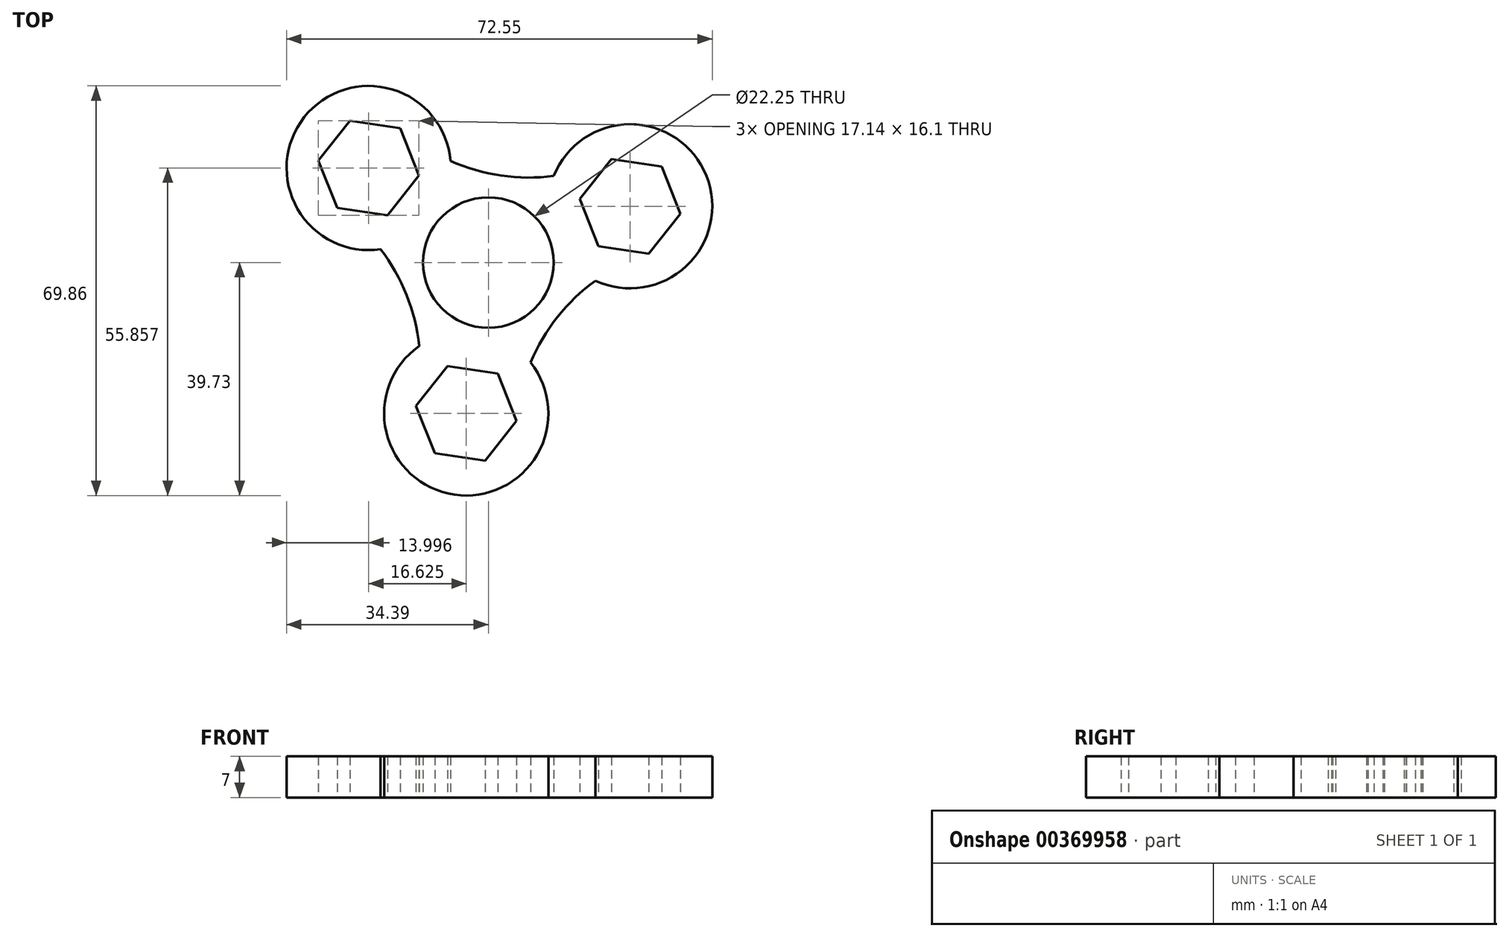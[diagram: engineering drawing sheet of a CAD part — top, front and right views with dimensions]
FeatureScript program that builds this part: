
annotation { "Feature Type Name" : "Feature", "Feature Type Description" : "" }
export const myFeature = defineFeature(function(context is Context, id is Id, definition is map)
    precondition{}
    {
        {
            var Q0;
            Q0=qCreatedBy(makeId("Top.planeOp"),FACE);
            var sketch = newSketch(context, id + "F0", { "sketchPlane" : qUnion([Q0])});
            skCircle(sketch, "E0", {"center": v(0, 0) * mm, "radius": 15 * mm});
            skCircle(sketch, "E1", {"center": v(0, 0) * mm, "radius": 11.12 * mm});
            skLineSegment(sketch, "E2", {"start": v(0, 0) * mm, "end": v(-20.4, 16.13) * mm});
            skLineSegment(sketch, "E3", {"start": v(0, 0) * mm, "end": v(24.16, 9.6) * mm});
            skLineSegment(sketch, "E4", {"start": v(0, 0) * mm, "end": v(-3.77, -25.73) * mm});
            skCircle(sketch, "E5.cCircle", {"center": v(-20.4, 16.13) * mm, "radius": 7.5 * mm, "construction": true});
            skLineSegment(sketch, "E5.0", {"start": v(-11.83, 14.87) * mm, "end": v(-17.2, 8.08) * mm});
            skLineSegment(sketch, "E5.1", {"start": v(-17.2, 8.08) * mm, "end": v(-25.77, 9.33) * mm});
            skLineSegment(sketch, "E5.2", {"start": v(-25.77, 9.33) * mm, "end": v(-28.96, 17.38) * mm});
            skLineSegment(sketch, "E5.3", {"start": v(-28.96, 17.38) * mm, "end": v(-23.6, 24.18) * mm});
            skLineSegment(sketch, "E5.4", {"start": v(-23.6, 24.18) * mm, "end": v(-15.02, 22.92) * mm});
            skLineSegment(sketch, "E5.5", {"start": v(-15.02, 22.92) * mm, "end": v(-11.83, 14.87) * mm});
            skPoint(sketch, "E5.0.midPoint", {"position": v(-14.51, 11.47) * mm});
            skCircle(sketch, "E6.cCircle", {"center": v(24.16, 9.6) * mm, "radius": 7.5 * mm, "construction": true});
            skLineSegment(sketch, "E6.0", {"start": v(18.8, 2.8) * mm, "end": v(15.6, 10.85) * mm});
            skLineSegment(sketch, "E6.1", {"start": v(15.6, 10.85) * mm, "end": v(20.97, 17.65) * mm});
            skLineSegment(sketch, "E6.2", {"start": v(20.97, 17.65) * mm, "end": v(29.54, 16.4) * mm});
            skLineSegment(sketch, "E6.3", {"start": v(29.54, 16.4) * mm, "end": v(32.73, 8.34) * mm});
            skLineSegment(sketch, "E6.4", {"start": v(32.73, 8.34) * mm, "end": v(27.36, 1.55) * mm});
            skLineSegment(sketch, "E6.5", {"start": v(27.36, 1.55) * mm, "end": v(18.8, 2.8) * mm});
            skPoint(sketch, "E6.0.midPoint", {"position": v(17.2, 6.83) * mm});
            skCircle(sketch, "E7.cCircle", {"center": v(-3.77, -25.73) * mm, "radius": 7.5 * mm, "construction": true});
            skLineSegment(sketch, "E7.0", {"start": v(-6.97, -17.68) * mm, "end": v(1.6, -18.93) * mm});
            skLineSegment(sketch, "E7.1", {"start": v(1.6, -18.93) * mm, "end": v(4.8, -26.98) * mm});
            skLineSegment(sketch, "E7.2", {"start": v(4.8, -26.98) * mm, "end": v(-0.57, -33.77) * mm});
            skLineSegment(sketch, "E7.3", {"start": v(-0.57, -33.77) * mm, "end": v(-9.14, -32.52) * mm});
            skLineSegment(sketch, "E7.4", {"start": v(-9.14, -32.52) * mm, "end": v(-12.34, -24.47) * mm});
            skLineSegment(sketch, "E7.5", {"start": v(-12.34, -24.47) * mm, "end": v(-6.97, -17.68) * mm});
            skPoint(sketch, "E7.0.midPoint", {"position": v(-2.68, -18.3) * mm});
            skArc(sketch, "E8", {"start": v(-15.02, 22.92) * mm, "mid": v(2.17, 14.84) * mm, "end": v(20.97, 17.65) * mm});
            skArc(sketch, "E9", {"start": v(27.36, 1.55) * mm, "mid": v(11.77, -9.3) * mm, "end": v(4.8, -26.98) * mm});
            skArc(sketch, "E10", {"start": v(-12.34, -24.47) * mm, "mid": v(-13.94, -5.54) * mm, "end": v(-25.77, 9.33) * mm});
            skCircle(sketch, "E11", {"center": v(-3.77, -25.73) * mm, "radius": 14 * mm});
            skCircle(sketch, "E12", {"center": v(-20.4, 16.13) * mm, "radius": 14 * mm});
            skCircle(sketch, "E13", {"center": v(24.16, 9.6) * mm, "radius": 14 * mm});
            skSolve(sketch);
        }
        {
            var Q0;
            {var subQ0=sQuery(id+"F0.wireOp",EDGE,"E8");var subQ1=sQuery(id+"F0.wireOp",EDGE,"E0");var subQ2=makeQuery(id+"F0.imprint","INTERSECT",VERTEX,{"derivedFrom":[subQ1,subQ0]});Q0=makeQuery(id+"F0.imprint","IMPRINT",FACE,{"disambiguationData":[TD([[makeQuery(id+"F0.imprint","IMPRINT",EDGE,{"disambiguationData":[TD([[subQ2,1.0]])],"derivedFrom":subQ1}),-1.0]])]});}
            var Q1;
            {var subQ0=sQuery(id+"F0.wireOp",EDGE,"E8");var subQ1=sQuery(id+"F0.wireOp",EDGE,"E0");var subQ2=makeQuery(id+"F0.imprint","INTERSECT",VERTEX,{"derivedFrom":[subQ1,subQ0]});Q1=makeQuery(id+"F0.imprint","IMPRINT",FACE,{"disambiguationData":[TD([[makeQuery(id+"F0.imprint","IMPRINT",EDGE,{"disambiguationData":[TD([[subQ2,-1.0]])],"derivedFrom":subQ1}),-1.0]])]});}
            var Q2;
            {var subQ0=sQuery(id+"F0.wireOp",EDGE,"E10");var subQ1=sQuery(id+"F0.wireOp",EDGE,"E0");var subQ2=makeQuery(id+"F0.imprint","INTERSECT",VERTEX,{"derivedFrom":[subQ1,subQ0]});Q2=makeQuery(id+"F0.imprint","IMPRINT",FACE,{"disambiguationData":[TD([[makeQuery(id+"F0.imprint","IMPRINT",EDGE,{"disambiguationData":[TD([[subQ2,1.0]])],"derivedFrom":subQ1}),-1.0]])]});}
            var Q3;
            {var subQ0=sQuery(id+"F0.wireOp",EDGE,"E10");var subQ1=sQuery(id+"F0.wireOp",EDGE,"E0");var subQ2=makeQuery(id+"F0.imprint","INTERSECT",VERTEX,{"derivedFrom":[subQ1,subQ0]});Q3=makeQuery(id+"F0.imprint","IMPRINT",FACE,{"disambiguationData":[TD([[makeQuery(id+"F0.imprint","IMPRINT",EDGE,{"disambiguationData":[TD([[subQ2,-1.0]])],"derivedFrom":subQ1}),-1.0]])]});}
            var Q4;
            {var subQ0=sQuery(id+"F0.wireOp",EDGE,"E9");var subQ1=sQuery(id+"F0.wireOp",EDGE,"E0");var subQ2=makeQuery(id+"F0.imprint","INTERSECT",VERTEX,{"derivedFrom":[subQ1,subQ0]});Q4=makeQuery(id+"F0.imprint","IMPRINT",FACE,{"disambiguationData":[TD([[makeQuery(id+"F0.imprint","IMPRINT",EDGE,{"disambiguationData":[TD([[subQ2,1.0]])],"derivedFrom":subQ1}),-1.0]])]});}
            var Q5;
            {var subQ0=sQuery(id+"F0.wireOp",EDGE,"E9");var subQ1=sQuery(id+"F0.wireOp",EDGE,"E0");var subQ2=makeQuery(id+"F0.imprint","INTERSECT",VERTEX,{"derivedFrom":[subQ1,subQ0]});Q5=makeQuery(id+"F0.imprint","IMPRINT",FACE,{"disambiguationData":[TD([[makeQuery(id+"F0.imprint","IMPRINT",EDGE,{"disambiguationData":[TD([[subQ2,-1.0]])],"derivedFrom":subQ1}),-1.0]])]});}
            var Q6;
            {var subQ5=sQuery(id+"F0.wireOp",EDGE,"E5.2");Q6=makeQuery(id+"F0.imprint","IMPRINT",FACE,{"disambiguationData":[TD([[makeQuery(id+"F0.imprint","IMPRINT",EDGE,{"derivedFrom":subQ5}),1.0]])]});}
            var Q7;
            {var subQ1=sQuery(id+"F0.wireOp",EDGE,"E6.2");Q7=makeQuery(id+"F0.imprint","IMPRINT",FACE,{"disambiguationData":[TD([[makeQuery(id+"F0.imprint","IMPRINT",EDGE,{"derivedFrom":subQ1}),1.0]])]});}
            var Q8;
            {var subQ2=sQuery(id+"F0.wireOp",EDGE,"E7.2");Q8=makeQuery(id+"F0.imprint","IMPRINT",FACE,{"disambiguationData":[TD([[makeQuery(id+"F0.imprint","IMPRINT",EDGE,{"derivedFrom":subQ2}),1.0]])]});}
            var Q9;
            {var subQ0=sQuery(id+"F0.wireOp",EDGE,"E6.5");Q9=makeQuery(id+"F0.imprint","IMPRINT",FACE,{"disambiguationData":[TD([[makeQuery(id+"F0.imprint","IMPRINT",EDGE,{"derivedFrom":subQ0}),1.0]])]});}
            var Q10;
            {var subQ0=sQuery(id+"F0.wireOp",EDGE,"E6.1");Q10=makeQuery(id+"F0.imprint","IMPRINT",FACE,{"disambiguationData":[TD([[makeQuery(id+"F0.imprint","IMPRINT",EDGE,{"derivedFrom":subQ0}),1.0]])]});}
            var Q11;
            {var subQ0=sQuery(id+"F0.wireOp",EDGE,"E5.5");Q11=makeQuery(id+"F0.imprint","IMPRINT",FACE,{"disambiguationData":[TD([[makeQuery(id+"F0.imprint","IMPRINT",EDGE,{"derivedFrom":subQ0}),1.0]])]});}
            var Q12;
            {var subQ0=sQuery(id+"F0.wireOp",EDGE,"E5.1");Q12=makeQuery(id+"F0.imprint","IMPRINT",FACE,{"disambiguationData":[TD([[makeQuery(id+"F0.imprint","IMPRINT",EDGE,{"derivedFrom":subQ0}),1.0]])]});}
            var Q13;
            {var subQ0=sQuery(id+"F0.wireOp",EDGE,"E7.5");Q13=makeQuery(id+"F0.imprint","IMPRINT",FACE,{"disambiguationData":[TD([[makeQuery(id+"F0.imprint","IMPRINT",EDGE,{"derivedFrom":subQ0}),1.0]])]});}
            var Q14;
            {var subQ0=sQuery(id+"F0.wireOp",EDGE,"E7.1");Q14=makeQuery(id+"F0.imprint","IMPRINT",FACE,{"disambiguationData":[TD([[makeQuery(id+"F0.imprint","IMPRINT",EDGE,{"derivedFrom":subQ0}),1.0]])]});}
            var Q15;
            {var subQ6=sQuery(id+"F0.wireOp",EDGE,"E0");var subQ10=makeQuery(id+"F0.imprint","INTERSECT",VERTEX,{"derivedFrom":[subQ6,sQuery(id+"F0.wireOp",EDGE,"E8")]});Q15=makeQuery(id+"F0.imprint","IMPRINT",FACE,{"disambiguationData":[TD([[makeQuery(id+"F0.imprint","IMPRINT",EDGE,{"disambiguationData":[TD([[subQ10,1.0]])],"derivedFrom":subQ6}),1.0]])]});}
            var Q16;
            {var subQ5=sQuery(id+"F0.wireOp",EDGE,"E0");var subQ6=makeQuery(id+"F0.imprint","INTERSECT",VERTEX,{"derivedFrom":[subQ5,sQuery(id+"F0.wireOp",EDGE,"E9")]});Q16=makeQuery(id+"F0.imprint","IMPRINT",FACE,{"disambiguationData":[TD([[makeQuery(id+"F0.imprint","IMPRINT",EDGE,{"disambiguationData":[TD([[subQ6,1.0]])],"derivedFrom":subQ5}),1.0]])]});}
            var Q17;
            {var subQ0=sQuery(id+"F0.wireOp",EDGE,"E12");var subQ1=sQuery(id+"F0.wireOp",EDGE,"E0");var subQ2=makeQuery(id+"F0.imprint","INTERSECT",VERTEX,{"disambiguationData":[OD(0.0)],"derivedFrom":[subQ1,subQ0]});Q17=makeQuery(id+"F0.imprint","IMPRINT",FACE,{"disambiguationData":[TD([[makeQuery(id+"F0.imprint","IMPRINT",EDGE,{"disambiguationData":[TD([[subQ2,-1.0]])],"derivedFrom":subQ1}),1.0]])]});}
            var Q18;
            {var subQ0=sQuery(id+"F0.wireOp",EDGE,"E2");var subQ1=sQuery(id+"F0.wireOp",EDGE,"E0");var subQ2=makeQuery(id+"F0.imprint","INTERSECT",VERTEX,{"derivedFrom":[subQ1,subQ0]});Q18=makeQuery(id+"F0.imprint","IMPRINT",FACE,{"disambiguationData":[TD([[makeQuery(id+"F0.imprint","IMPRINT",EDGE,{"disambiguationData":[TD([[subQ2,-1.0]])],"derivedFrom":subQ1}),1.0]])]});}
            var Q19;
            {var subQ0=sQuery(id+"F0.wireOp",EDGE,"E3");var subQ1=sQuery(id+"F0.wireOp",EDGE,"E0");var subQ2=makeQuery(id+"F0.imprint","INTERSECT",VERTEX,{"derivedFrom":[subQ1,subQ0]});Q19=makeQuery(id+"F0.imprint","IMPRINT",FACE,{"disambiguationData":[TD([[makeQuery(id+"F0.imprint","IMPRINT",EDGE,{"disambiguationData":[TD([[subQ2,1.0]])],"derivedFrom":subQ1}),1.0]])]});}
            var Q20;
            {var subQ7=sQuery(id+"F0.wireOp",EDGE,"E0");var subQ8=makeQuery(id+"F0.imprint","INTERSECT",VERTEX,{"derivedFrom":[subQ7,sQuery(id+"F0.wireOp",EDGE,"E10")]});Q20=makeQuery(id+"F0.imprint","IMPRINT",FACE,{"disambiguationData":[TD([[makeQuery(id+"F0.imprint","IMPRINT",EDGE,{"disambiguationData":[TD([[subQ8,1.0]])],"derivedFrom":subQ7}),1.0]])]});}
            var Q21;
            {var subQ0=sQuery(id+"F0.wireOp",EDGE,"E11");var subQ1=sQuery(id+"F0.wireOp",EDGE,"E0");var subQ2=makeQuery(id+"F0.imprint","INTERSECT",VERTEX,{"disambiguationData":[OD(0.0)],"derivedFrom":[subQ1,subQ0]});Q21=makeQuery(id+"F0.imprint","IMPRINT",FACE,{"disambiguationData":[TD([[makeQuery(id+"F0.imprint","IMPRINT",EDGE,{"disambiguationData":[TD([[subQ2,-1.0]])],"derivedFrom":subQ1}),1.0]])]});}
            var Q22;
            {var subQ0=sQuery(id+"F0.wireOp",EDGE,"E4");var subQ1=sQuery(id+"F0.wireOp",EDGE,"E0");var subQ2=makeQuery(id+"F0.imprint","INTERSECT",VERTEX,{"derivedFrom":[subQ1,subQ0]});Q22=makeQuery(id+"F0.imprint","IMPRINT",FACE,{"disambiguationData":[TD([[makeQuery(id+"F0.imprint","IMPRINT",EDGE,{"disambiguationData":[TD([[subQ2,-1.0]])],"derivedFrom":subQ1}),1.0]])]});}
            var Q23;
            {var subQ0=sQuery(id+"F0.wireOp",EDGE,"E3");var subQ1=sQuery(id+"F0.wireOp",EDGE,"E0");var subQ2=makeQuery(id+"F0.imprint","INTERSECT",VERTEX,{"derivedFrom":[subQ1,subQ0]});Q23=makeQuery(id+"F0.imprint","IMPRINT",FACE,{"disambiguationData":[TD([[makeQuery(id+"F0.imprint","IMPRINT",EDGE,{"disambiguationData":[TD([[subQ2,-1.0]])],"derivedFrom":subQ1}),1.0]])]});}
            extrude(context, id + "F1", {"entities" : qUnion([Q0, Q1, Q2, Q3, Q4, Q5, Q6, Q7, Q8, Q9, Q10, Q11, Q12, Q13, Q14, Q15, Q16, Q17, Q18, Q19, Q20, Q21, Q22, Q23]), "depth" : 7 * mm});
        }
    });
